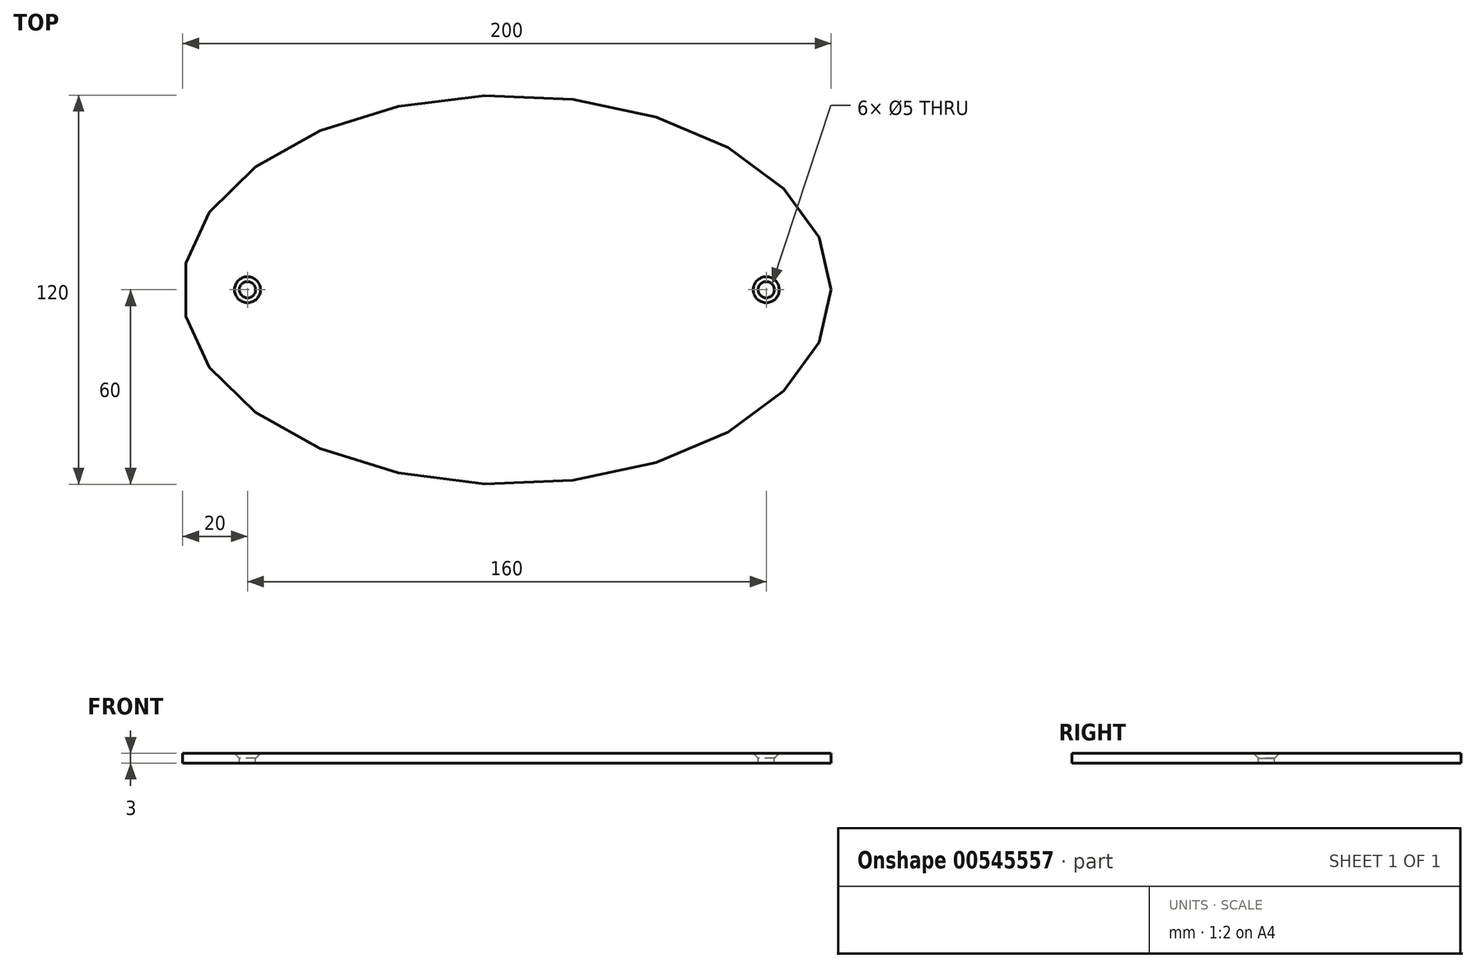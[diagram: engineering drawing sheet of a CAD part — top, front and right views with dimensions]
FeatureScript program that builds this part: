
annotation { "Feature Type Name" : "Feature", "Feature Type Description" : "" }
export const myFeature = defineFeature(function(context is Context, id is Id, definition is map)
    precondition{}
    {
        {
            var Q0;
            Q0=qCreatedBy(makeId("Top.planeOp"),FACE);
            var sketch = newSketch(context, id + "F0", { "sketchPlane" : qUnion([Q0])});
            skEllipse(sketch, "E0", {"center": v(0, 0) * mm, "majorRadius": 100 * mm, "minorRadius": 60 * mm, "majorAxis": v(1, 0)});
            skSolve(sketch);
        }
        {
            var Q0;
            Q0=makeQuery(id+"F0.imprint","IMPRINT",FACE,{"disambiguationData":[TD([[makeQuery(id+"F0.imprint","IMPRINT",EDGE,{"derivedFrom":sQuery(id+"F0.wireOp",EDGE,"E0")}),1.0]])]});
            extrude(context, id + "F1", {"entities" : qUnion([Q0]), "oppositeDirection" : true, "depth" : 3 * mm, "offsetDistance" : 25 * mm});
        }
        {
            var Q0;
            Q0=makeQuery(id+"F1.opExtrude","CAP_FACE",FACE,{"disambiguationData":[OSD([sQuery(id+"F0.wireOp",EDGE,"E0")])],"isStart":true});
            var sketch = newSketch(context, id + "F2", { "sketchPlane" : qUnion([Q0])});
            skPoint(sketch, "E1", {"position": v(-80, 0) * mm});
            skPoint(sketch, "E2", {"position": v(80, 0) * mm});
            skSolve(sketch);
        }
        {
            var Q0;
            Q0=sQuery(id+"F2.wireOp",VERTEX,"E1");
            var Q1;
            Q1=sQuery(id+"F2.wireOp",VERTEX,"E2");
            var Q2;
            Q2=makeQuery(id+"F1.opExtrude","SWEPT_BODY",BODY,{"disambiguationData":[OSD([sQuery(id+"F0.wireOp",EDGE,"E0")])]});
            hole(context, id + "F3", {"style" : HoleStyle.C_SINK, "endStyle" : HoleEndStyle.THROUGH, "holeDiameter" : 5 * mm, "cSinkDiameter" : 8 * mm, "cSinkAngle" : 90 * degree, "majorDiameter" : 5 * mm, "isTappedThrough" : true, "tappedDepth" : 12 * mm, "tapClearance" : 3, "locations" : qUnion([Q0, Q1]), "scope" : qUnion([Q2])});
        }
    });
